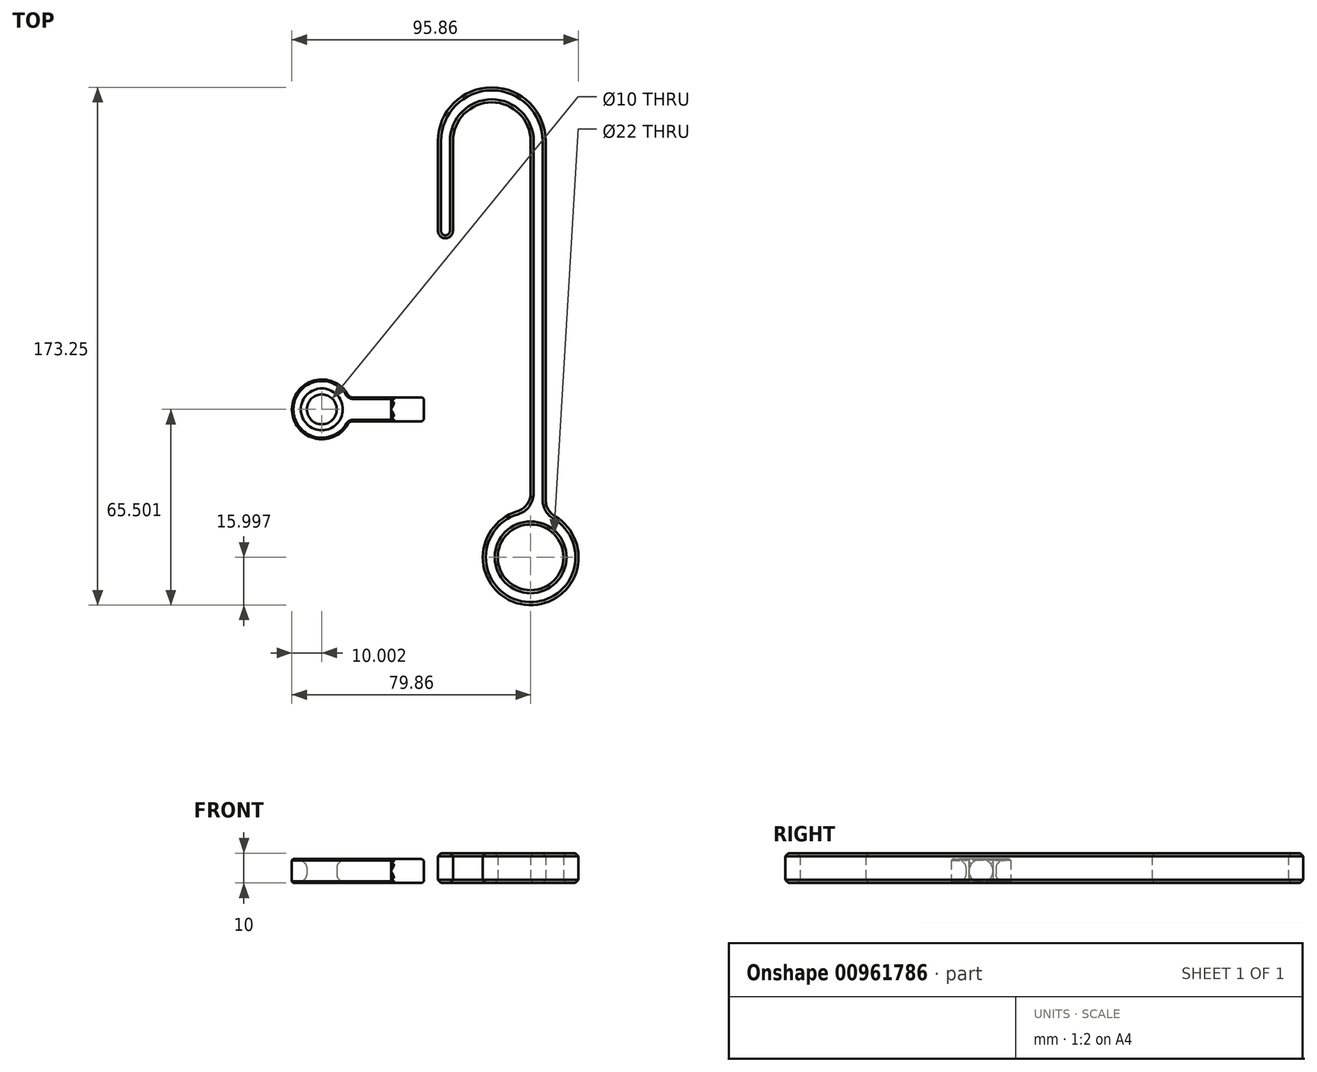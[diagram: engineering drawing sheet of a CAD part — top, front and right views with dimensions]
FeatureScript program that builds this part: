
annotation { "Feature Type Name" : "Feature", "Feature Type Description" : "" }
export const myFeature = defineFeature(function(context is Context, id is Id, definition is map)
    precondition{}
    {
        {
            var Q0;
            Q0=qCreatedBy(makeId("Top.planeOp"),FACE);
            var sketch = newSketch(context, id + "F0", { "sketchPlane" : qUnion([Q0])});
            skCircle(sketch, "E0", {"center": v(0, 54.02) * mm, "radius": 13 * mm, "construction": true});
            skArc(sketch, "E1", {"start": v(18, 54.02) * mm, "mid": v(0, 72.02) * mm, "end": v(-18, 54.02) * mm});
            skLineSegment(sketch, "E2", {"start": v(-18, 54.02) * mm, "end": v(-18, 24.02) * mm});
            skLineSegment(sketch, "E3", {"start": v(18, 54.02) * mm, "end": v(18, -65.98) * mm});
            skLineSegment(sketch, "E4.0", {"start": v(-13, 54.02) * mm, "end": v(-13, 24.02) * mm});
            skArc(sketch, "E4.1", {"start": v(13, 54.02) * mm, "mid": v(0, 67.02) * mm, "end": v(-13, 54.02) * mm});
            skLineSegment(sketch, "E4.2", {"start": v(13, 54.02) * mm, "end": v(13, -63.8) * mm});
            skCircle(sketch, "E5", {"center": v(13, -85.23) * mm, "radius": 11 * mm});
            skArc(sketch, "E6.0", {"start": v(8.45, -69.9) * mm, "mid": v(11.05, -101.11) * mm, "end": v(21.13, -71.45) * mm});
            skArc(sketch, "E7", {"start": v(-18, 24.02) * mm, "mid": v(-15.5, 21.52) * mm, "end": v(-13, 24.02) * mm});
            skPoint(sketch, "E8.visualSharp", {"position": v(13, -69.23) * mm});
            skArc(sketch, "E8.filletArc", {"start": v(8.45, -69.9) * mm, "mid": v(11.74, -67.6) * mm, "end": v(13, -63.8) * mm});
            skPoint(sketch, "E9.visualSharp", {"position": v(18, -70.03) * mm});
            skArc(sketch, "E9.filletArc", {"start": v(18, -65.98) * mm, "mid": v(18.84, -69.13) * mm, "end": v(21.13, -71.45) * mm});
            skSolve(sketch);
        }
        {
            var Q0;
            Q0=makeQuery(id+"F0.imprint","IMPRINT",FACE,{"disambiguationData":[TD([[makeQuery(id+"F0.imprint","IMPRINT",EDGE,{"derivedFrom":sQuery(id+"F0.wireOp",EDGE,"E1")}),1.0]])]});
            extrude(context, id + "F1", {"entities" : qUnion([Q0]), "depth" : 10 * mm, "offsetDistance" : 25 * mm});
        }
        {
            var Q0;
            Q0=qCreatedBy(makeId("Top.planeOp"),FACE);
            var sketch = newSketch(context, id + "F2", { "sketchPlane" : qUnion([Q0])});
            skCircle(sketch, "E10", {"center": v(-56.86, -35.73) * mm, "radius": 5 * mm});
            skLineSegment(sketch, "E11.0", {"start": v(-47.7, -39.73) * mm, "end": v(-22.7, -39.73) * mm});
            skLineSegment(sketch, "E12.0", {"start": v(-47.7, -31.73) * mm, "end": v(-22.7, -31.73) * mm});
            skCircle(sketch, "E13.0", {"center": v(-56.86, -35.73) * mm, "radius": 10 * mm});
            skLineSegment(sketch, "E14", {"start": v(-22.7, -31.73) * mm, "end": v(-22.7, -39.73) * mm});
            skSolve(sketch);
        }
        {
            var Q0;
            Q0=makeQuery(id+"F2.imprint","IMPRINT",FACE,{"disambiguationData":[TD([[makeQuery(id+"F2.imprint","IMPRINT",EDGE,{"derivedFrom":sQuery(id+"F2.wireOp",EDGE,"E10")}),-1.0]])]});
            var Q1;
            {var subQ1=sQuery(id+"F2.wireOp",EDGE,"E11.0");Q1=makeQuery(id+"F2.imprint","IMPRINT",FACE,{"disambiguationData":[TD([[makeQuery(id+"F2.imprint","IMPRINT",EDGE,{"derivedFrom":subQ1}),1.0]])]});}
            extrude(context, id + "F3", {"entities" : qUnion([Q0, Q1]), "depth" : 8 * mm, "offsetDistance" : 25 * mm});
        }
        {
            var Q0;
            Q0=makeQuery(id+"F3.opExtrude","SWEPT_FACE",FACE,{"disambiguationData":[OSD([sQuery(id+"F2.wireOp",EDGE,"E14")])]});
            var sketch = newSketch(context, id + "F4", { "sketchPlane" : qUnion([Q0])});
            skCircle(sketch, "E15", {"center": v(-35.73, 4) * mm, "radius": 4 * mm});
            skPoint(sketch, "E15.centerSnap0", {"position": v(-35.73, 8) * mm});
            skPoint(sketch, "E15.centerSnap1", {"position": v(-31.73, 4) * mm});
            skSolve(sketch);
        }
        {
            var Q0;
            {var subQ0=sQuery(id+"F4.wireOp",EDGE,"E15");var subQ1=sQuery(id+"F2.wireOp",EDGE,"E14");var subQ2=makeQuery(id+"F3.opExtrude","CAP_EDGE",EDGE,{"disambiguationData":[OSD([subQ1])],"isStart":false});var subQ3=makeQuery(id+"F4.imprint","INTERSECT",VERTEX,{"derivedFrom":[subQ2,subQ0]});Q0=makeQuery(id+"F4.imprint","IMPRINT",FACE,{"disambiguationData":[TD([[makeQuery(id+"F4.imprint","IMPRINT",EDGE,{"disambiguationData":[TD([[subQ3,1.0]])],"derivedFrom":subQ0}),-1.0]])]});}
            var Q1;
            {var subQ0=sQuery(id+"F4.wireOp",EDGE,"E15");var subQ1=sQuery(id+"F2.wireOp",EDGE,"E14");var subQ4=makeQuery(id+"F3.opExtrude","CAP_EDGE",EDGE,{"disambiguationData":[OSD([subQ1])],"isStart":true});var subQ5=makeQuery(id+"F4.imprint","INTERSECT",VERTEX,{"derivedFrom":[subQ4,subQ0]});Q1=makeQuery(id+"F4.imprint","IMPRINT",FACE,{"disambiguationData":[TD([[makeQuery(id+"F4.imprint","IMPRINT",EDGE,{"disambiguationData":[TD([[subQ5,-1.0]])],"derivedFrom":subQ0}),-1.0]])]});}
            var Q2;
            {var subQ0=sQuery(id+"F4.wireOp",EDGE,"E15");var subQ1=sQuery(id+"F2.wireOp",EDGE,"E14");var subQ4=makeQuery(id+"F3.opExtrude","CAP_EDGE",EDGE,{"disambiguationData":[OSD([subQ1])],"isStart":true});var subQ5=makeQuery(id+"F4.imprint","INTERSECT",VERTEX,{"derivedFrom":[subQ4,subQ0]});Q2=makeQuery(id+"F4.imprint","IMPRINT",FACE,{"disambiguationData":[TD([[makeQuery(id+"F4.imprint","IMPRINT",EDGE,{"disambiguationData":[TD([[subQ5,1.0]])],"derivedFrom":subQ0}),-1.0]])]});}
            var Q3;
            {var subQ0=sQuery(id+"F4.wireOp",EDGE,"E15");var subQ1=sQuery(id+"F2.wireOp",EDGE,"E14");var subQ2=makeQuery(id+"F3.opExtrude","CAP_EDGE",EDGE,{"disambiguationData":[OSD([subQ1])],"isStart":false});var subQ3=makeQuery(id+"F4.imprint","INTERSECT",VERTEX,{"derivedFrom":[subQ2,subQ0]});Q3=makeQuery(id+"F4.imprint","IMPRINT",FACE,{"disambiguationData":[TD([[makeQuery(id+"F4.imprint","IMPRINT",EDGE,{"disambiguationData":[TD([[subQ3,-1.0]])],"derivedFrom":subQ0}),-1.0]])]});}
            extrude(context, id + "F5", {"entities" : qUnion([Q0, Q1, Q2, Q3]), "operationType" : NewBodyOperationType.REMOVE, "oppositeDirection" : true, "depth" : 11 * mm, "offsetDistance" : 25 * mm});
        }
        {
            var Q0;
            {var subQ0=sQuery(id+"F4.wireOp",EDGE,"E15");var subQ1=sQuery(id+"F2.wireOp",EDGE,"E14");var subQ3=makeQuery(id+"F4.imprint","INTERSECT",VERTEX,{"derivedFrom":[makeQuery(id+"F3.opExtrude","CAP_EDGE",EDGE,{"disambiguationData":[OSD([subQ1])],"isStart":true}),subQ0]});var subQ5=makeQuery(id+"F4.imprint","INTERSECT",VERTEX,{"derivedFrom":[makeQuery(id+"F3.opExtrude","CAP_EDGE",EDGE,{"disambiguationData":[OSD([subQ1])],"isStart":false}),subQ0]});Q0=makeQuery(id+"F5.boolean.opBoolean","MERGE",FACE,{"derivedFrom":[],"fromTools":[makeQuery(id+"F5.opExtrude","SWEPT_FACE",FACE,{"disambiguationData":[OSD([subQ0]),TDD([makeQuery(id+"F4.imprint","IMPRINT",EDGE,{"disambiguationData":[TD([[subQ5,1.0]])],"derivedFrom":subQ0})])]}),makeQuery(id+"F5.opExtrude","SWEPT_FACE",FACE,{"disambiguationData":[OSD([subQ0]),TDD([makeQuery(id+"F4.imprint","IMPRINT",EDGE,{"disambiguationData":[TD([[subQ5,-1.0]])],"derivedFrom":subQ0})])]}),makeQuery(id+"F5.opExtrude","SWEPT_FACE",FACE,{"disambiguationData":[OSD([subQ0]),TDD([makeQuery(id+"F4.imprint","IMPRINT",EDGE,{"disambiguationData":[TD([[subQ3,1.0]])],"derivedFrom":subQ0})])]}),makeQuery(id+"F5.opExtrude","SWEPT_FACE",FACE,{"disambiguationData":[OSD([subQ0]),TDD([makeQuery(id+"F4.imprint","IMPRINT",EDGE,{"disambiguationData":[TD([[subQ3,-1.0]])],"derivedFrom":subQ0})])]})]});}
            fillet(context, id + "F6", {"entities" : qUnion([Q0]), "tangentPropagation" : true, "radius" : 1 * mm, "defaultsChanged" : false, "vertexSettings" : [], "allowEdgeOverflow" : false});
        }
        {
            var Q0;
            Q0=makeQuery(id+"F3.opExtrude","CAP_EDGE",EDGE,{"disambiguationData":[OSD([sQuery(id+"F2.wireOp",EDGE,"E10")])],"isStart":true});
            var Q1;
            Q1=makeQuery(id+"F3.opExtrude","CAP_EDGE",EDGE,{"disambiguationData":[OSD([sQuery(id+"F2.wireOp",EDGE,"E10")])],"isStart":false});
            chamfer(context, id + "F7", {"entities" : qUnion([Q0, Q1]), "width" : 2 * mm, "tangentPropagation" : true});
        }
        {
            var Q0;
            Q0=makeQuery(id+"F3.opExtrude","SWEPT_FACE",FACE,{"disambiguationData":[OSD([sQuery(id+"F2.wireOp",EDGE,"E10")])]});
            var Q1;
            Q1=makeQuery(id+"F3.opExtrude","SWEPT_EDGE",EDGE,{"disambiguationData":[OSD([sQuery(id+"F2.wireOp",EDGE,"E11.0"),sQuery(id+"F2.wireOp",EDGE,"E13.0")])]});
            var Q2;
            Q2=makeQuery(id+"F3.opExtrude","SWEPT_EDGE",EDGE,{"disambiguationData":[OSD([sQuery(id+"F2.wireOp",EDGE,"E12.0"),sQuery(id+"F2.wireOp",EDGE,"E13.0")])]});
            fillet(context, id + "F8", {"entities" : qUnion([Q0, Q1, Q2]), "tangentPropagation" : true, "radius" : 2 * mm, "defaultsChanged" : false, "vertexSettings" : [], "allowEdgeOverflow" : false});
        }
        {
            var Q0;
            Q0=makeQuery(id+"F1.opExtrude","CAP_FACE",FACE,{"disambiguationData":[OSD([sQuery(id+"F0.wireOp",EDGE,"E1"),sQuery(id+"F0.wireOp",EDGE,"E2"),sQuery(id+"F0.wireOp",EDGE,"E3"),sQuery(id+"F0.wireOp",EDGE,"E4.0"),sQuery(id+"F0.wireOp",EDGE,"E4.1"),sQuery(id+"F0.wireOp",EDGE,"E4.2"),sQuery(id+"F0.wireOp",EDGE,"E5"),sQuery(id+"F0.wireOp",EDGE,"E6.0"),sQuery(id+"F0.wireOp",EDGE,"E7"),sQuery(id+"F0.wireOp",EDGE,"E8.filletArc"),sQuery(id+"F0.wireOp",EDGE,"E9.filletArc")])],"isStart":false});
            var Q1;
            Q1=makeQuery(id+"F1.opExtrude","CAP_FACE",FACE,{"disambiguationData":[OSD([sQuery(id+"F0.wireOp",EDGE,"E1"),sQuery(id+"F0.wireOp",EDGE,"E2"),sQuery(id+"F0.wireOp",EDGE,"E3"),sQuery(id+"F0.wireOp",EDGE,"E4.0"),sQuery(id+"F0.wireOp",EDGE,"E4.1"),sQuery(id+"F0.wireOp",EDGE,"E4.2"),sQuery(id+"F0.wireOp",EDGE,"E5"),sQuery(id+"F0.wireOp",EDGE,"E6.0"),sQuery(id+"F0.wireOp",EDGE,"E7"),sQuery(id+"F0.wireOp",EDGE,"E8.filletArc"),sQuery(id+"F0.wireOp",EDGE,"E9.filletArc")])],"isStart":true});
            chamfer(context, id + "F9", {"entities" : qUnion([Q0, Q1]), "width" : 1 * mm, "tangentPropagation" : true});
        }
        {
            var Q0;
            Q0=makeQuery(id+"F3.opExtrude","CAP_EDGE",EDGE,{"disambiguationData":[OSD([sQuery(id+"F2.wireOp",EDGE,"E13.0")])],"isStart":false});
            var Q1;
            Q1=makeQuery(id+"F3.opExtrude","CAP_EDGE",EDGE,{"disambiguationData":[OSD([sQuery(id+"F2.wireOp",EDGE,"E13.0")])],"isStart":true});
            chamfer(context, id + "F10", {"entities" : qUnion([Q0, Q1]), "width" : 0.5 * mm, "tangentPropagation" : true});
        }
    });
